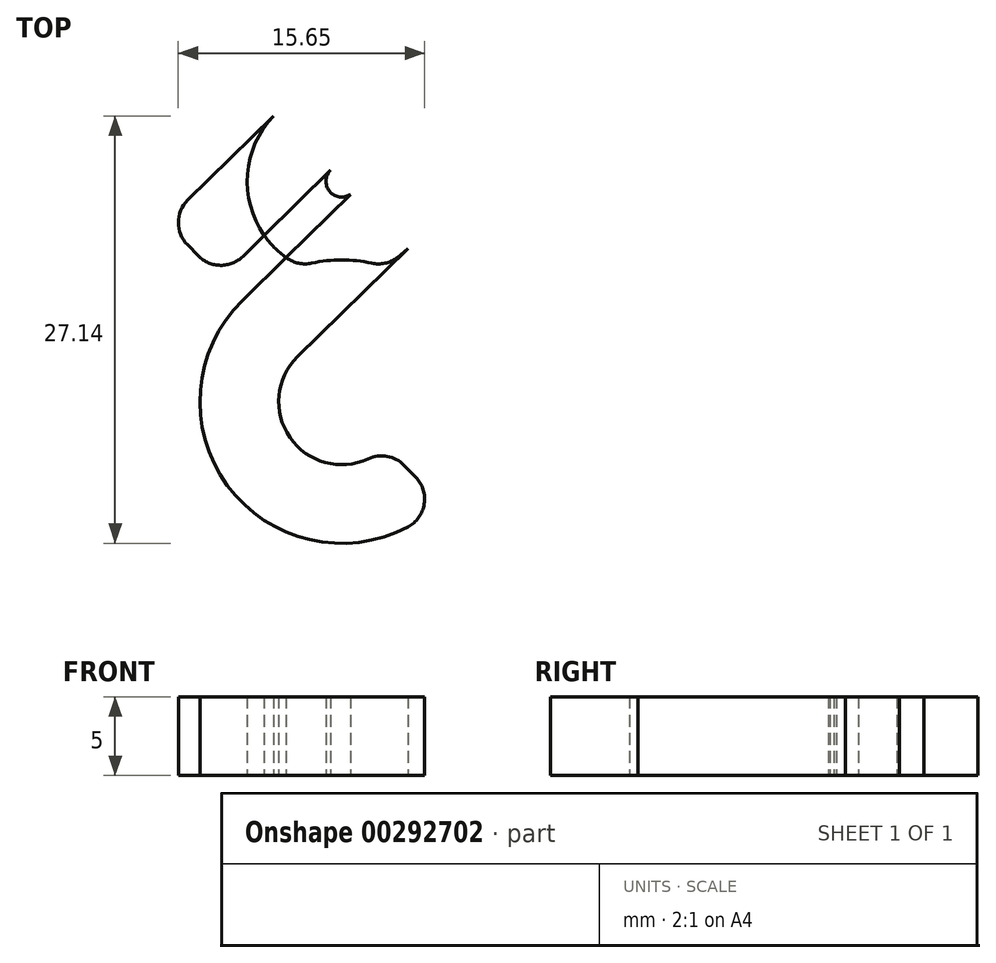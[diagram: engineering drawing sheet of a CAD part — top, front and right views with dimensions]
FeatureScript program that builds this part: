
annotation { "Feature Type Name" : "Feature", "Feature Type Description" : "" }
export const myFeature = defineFeature(function(context is Context, id is Id, definition is map)
    precondition{}
    {
        {
            var Q0;
            Q0=qCreatedBy(makeId("Top.planeOp"),FACE);
            var sketch = newSketch(context, id + "F0", { "sketchPlane" : qUnion([Q0])});
            skCircle(sketch, "E0", {"center": v(0, 4.29) * mm, "radius": 1 * mm});
            skCircle(sketch, "E1", {"center": v(0, -9.71) * mm, "radius": 4 * mm});
            skCircle(sketch, "E2.0", {"center": v(0, 4.29) * mm, "radius": 6 * mm});
            skCircle(sketch, "E3.0", {"center": v(0, -9.71) * mm, "radius": 9 * mm});
            skPoint(sketch, "E4", {"position": v(0, -0.71) * mm});
            skPoint(sketch, "E5", {"position": v(0, 3.29) * mm});
            skLineSegment(sketch, "E6", {"start": v(0.82, 3.71) * mm, "end": v(-6.3, -3.3) * mm});
            skLineSegment(sketch, "E7", {"start": v(-2.8, -6.86) * mm, "end": v(4.2, 0) * mm});
            skLineSegment(sketch, "E8", {"start": v(-6.3, -3.3) * mm, "end": v(-23.64, 14.33) * mm, "construction": true});
            skLineSegment(sketch, "E9", {"start": v(-11.2, 1.68) * mm, "end": v(-4.07, 8.7) * mm});
            skLineSegment(sketch, "E10", {"start": v(-7.7, -1.88) * mm, "end": v(-0.5, 5.2) * mm});
            skLineSegment(sketch, "E11", {"start": v(-11.2, 1.68) * mm, "end": v(-7.7, -1.88) * mm});
            skLineSegment(sketch, "E12", {"start": v(-2.8, -6.86) * mm, "end": v(12.96, -22.94) * mm, "construction": true});
            skLineSegment(sketch, "E13", {"start": v(2.8, -12.57) * mm, "end": v(6.3, -16.14) * mm});
            skSolve(sketch);
        }
        {
            var Q0;
            {var subQ0=sQuery(id+"F0.wireOp",EDGE,"UAE7EztI-776L-38RR-TcJO-34UUsvYv27rx");Q0=makeQuery(id+"F0.imprint","IMPRINT",FACE,{"disambiguationData":[TD([[makeQuery(id+"F0.imprint","IMPRINT",EDGE,{"derivedFrom":subQ0}),-1.0]])]});}
            var Q1;
            {var subQ0=sQuery(id+"F0.wireOp",EDGE,"E6");var subQ1=sQuery(id+"F0.wireOp",EDGE,"E2.0");var subQ2=makeQuery(id+"F0.imprint","INTERSECT",VERTEX,{"derivedFrom":[subQ1,subQ0]});Q1=makeQuery(id+"F0.imprint","IMPRINT",FACE,{"disambiguationData":[TD([[makeQuery(id+"F0.imprint","IMPRINT",EDGE,{"disambiguationData":[TD([[subQ2,-1.0]])],"derivedFrom":subQ1}),-1.0]])]});}
            var Q2;
            {var subQ0=sQuery(id+"F0.wireOp",EDGE,"E7");var subQ1=sQuery(id+"F0.wireOp",EDGE,"E2.0");var subQ2=makeQuery(id+"F0.imprint","INTERSECT",VERTEX,{"derivedFrom":[subQ1,subQ0]});Q2=makeQuery(id+"F0.imprint","IMPRINT",FACE,{"disambiguationData":[TD([[makeQuery(id+"F0.imprint","IMPRINT",EDGE,{"disambiguationData":[TD([[subQ2,1.0]])],"derivedFrom":subQ1}),-1.0]])]});}
            var Q3;
            {var subQ9=sQuery(id+"F0.wireOp",EDGE,"aU059WjH-SJCA-iRpA-wLCq-IoOA7b2Ukktb");Q3=makeQuery(id+"F0.imprint","IMPRINT",FACE,{"disambiguationData":[TD([[makeQuery(id+"F0.imprint","IMPRINT",EDGE,{"derivedFrom":subQ9}),-1.0]])]});}
            var Q4;
            {var subQ0=sQuery(id+"F0.wireOp",EDGE,"E6");var subQ5=sQuery(id+"F0.wireOp",EDGE,"E0");var subQ6=makeQuery(id+"F0.imprint","INTERSECT",VERTEX,{"disambiguationData":[OD(0.0)],"derivedFrom":[subQ5,subQ0]});Q4=makeQuery(id+"F0.imprint","IMPRINT",FACE,{"disambiguationData":[TD([[makeQuery(id+"F0.imprint","IMPRINT",EDGE,{"disambiguationData":[TD([[subQ6,1.0]])],"derivedFrom":subQ5}),-1.0]])]});}
            var Q5;
            {var subQ5=sQuery(id+"F0.wireOp",EDGE,"E11");Q5=makeQuery(id+"F0.imprint","IMPRINT",FACE,{"disambiguationData":[TD([[makeQuery(id+"F0.imprint","IMPRINT",EDGE,{"derivedFrom":subQ5}),1.0]])]});}
            var Q6;
            {var subQ0=sQuery(id+"F0.wireOp",EDGE,"E3.0");var subQ1=sQuery(id+"F0.wireOp",EDGE,"E2.0");var subQ2=makeQuery(id+"F0.imprint","INTERSECT",VERTEX,{"disambiguationData":[OD(0.0)],"derivedFrom":[subQ1,subQ0]});Q6=makeQuery(id+"F0.imprint","IMPRINT",FACE,{"disambiguationData":[TD([[makeQuery(id+"F0.imprint","IMPRINT",EDGE,{"disambiguationData":[TD([[subQ2,-1.0]])],"derivedFrom":subQ1}),1.0]])]});}
            var Q7;
            {var subQ9=sQuery(id+"F0.wireOp",EDGE,"E13");Q7=makeQuery(id+"F0.imprint","IMPRINT",FACE,{"disambiguationData":[TD([[makeQuery(id+"F0.imprint","IMPRINT",EDGE,{"derivedFrom":subQ9}),-1.0]])]});}
            extrude(context, id + "F1", {"entities" : qUnion([Q0, Q1, Q2, Q3, Q4, Q5, Q6, Q7]), "depth" : 5 * mm});
        }
        {
            var Q0;
            Q0=makeQuery(id+"F1.opExtrude","SWEPT_EDGE",EDGE,{"disambiguationData":[OSD([sQuery(id+"F0.wireOp",EDGE,"E1"),sQuery(id+"F0.wireOp",EDGE,"aU059WjH-SJCA-iRpA-wLCq-IoOA7b2Ukktb")])]});
            var Q1;
            Q1=makeQuery(id+"F1.opExtrude","SWEPT_EDGE",EDGE,{"disambiguationData":[OSD([sQuery(id+"F0.wireOp",EDGE,"E3.0"),sQuery(id+"F0.wireOp",EDGE,"aU059WjH-SJCA-iRpA-wLCq-IoOA7b2Ukktb")])]});
            fillet(context, id + "F2", {"entities" : qUnion([Q0, Q1]), "radius" : 2 * mm, "tangentPropagation" : true, "allowEdgeOverflow" : false});
        }
        {
            var Q0;
            Q0=makeQuery(id+"F1.opExtrude","SWEPT_EDGE",EDGE,{"disambiguationData":[OSD([sQuery(id+"F0.wireOp",EDGE,"E9"),sQuery(id+"F0.wireOp",EDGE,"E11")])]});
            var Q1;
            Q1=makeQuery(id+"F1.opExtrude","SWEPT_EDGE",EDGE,{"disambiguationData":[OSD([sQuery(id+"F0.wireOp",EDGE,"E10"),sQuery(id+"F0.wireOp",EDGE,"E11")])]});
            fillet(context, id + "F3", {"entities" : qUnion([Q0, Q1]), "radius" : 2 * mm, "tangentPropagation" : true, "allowEdgeOverflow" : false});
        }
    });
